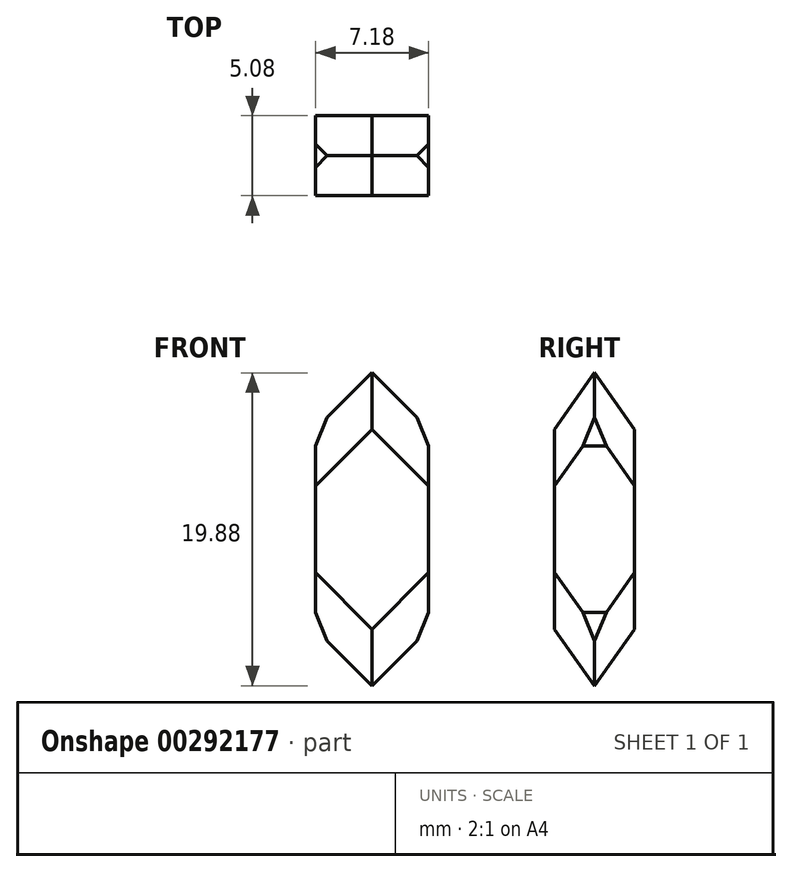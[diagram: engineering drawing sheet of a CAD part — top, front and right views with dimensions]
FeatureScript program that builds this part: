
annotation { "Feature Type Name" : "Feature", "Feature Type Description" : "" }
export const myFeature = defineFeature(function(context is Context, id is Id, definition is map)
    precondition{}
    {
        {
            var Q0;
            Q0=qCreatedBy(makeId("Front.planeOp"),FACE);
            var sketch = newSketch(context, id + "F0", { "sketchPlane" : qUnion([Q0])});
            skLineSegment(sketch, "E0", {"start": v(-22.12, 0) * mm, "end": v(-18.53, 3.6) * mm});
            skLineSegment(sketch, "E1", {"start": v(-18.53, 3.6) * mm, "end": v(-18.53, 16.3) * mm});
            skLineSegment(sketch, "E2", {"start": v(-18.53, 16.3) * mm, "end": v(-22.12, 19.88) * mm});
            skLineSegment(sketch, "E3", {"start": v(-22.12, 19.88) * mm, "end": v(-25.71, 16.3) * mm});
            skLineSegment(sketch, "E4", {"start": v(-25.71, 16.3) * mm, "end": v(-25.71, 3.6) * mm});
            skLineSegment(sketch, "E5", {"start": v(-25.71, 3.6) * mm, "end": v(-22.12, 0) * mm});
            skSolve(sketch);
        }
        {
            var Q0;
            Q0 = qSketchRegion(id + "F0", true);
            extrude(context, id + "F1", {"entities" : qUnion([Q0]), "depth" : 5.08 * mm});
        }
        {
            var Q0;
            Q0=makeQuery(id+"F1.opExtrude","CAP_EDGE",EDGE,{"disambiguationData":[OSD([sQuery(id+"F0.wireOp",EDGE,"E2")])],"isStart":false});
            var Q1;
            Q1=makeQuery(id+"F1.opExtrude","CAP_EDGE",EDGE,{"disambiguationData":[OSD([sQuery(id+"F0.wireOp",EDGE,"E3")])],"isStart":false});
            var Q2;
            Q2=makeQuery(id+"F1.opExtrude","CAP_EDGE",EDGE,{"disambiguationData":[OSD([sQuery(id+"F0.wireOp",EDGE,"E5")])],"isStart":false});
            var Q3;
            Q3=makeQuery(id+"F1.opExtrude","CAP_EDGE",EDGE,{"disambiguationData":[OSD([sQuery(id+"F0.wireOp",EDGE,"E0")])],"isStart":false});
            var Q4;
            Q4=makeQuery(id+"F1.opExtrude","CAP_EDGE",EDGE,{"disambiguationData":[OSD([sQuery(id+"F0.wireOp",EDGE,"E2")])],"isStart":true});
            var Q5;
            Q5=makeQuery(id+"F1.opExtrude","CAP_EDGE",EDGE,{"disambiguationData":[OSD([sQuery(id+"F0.wireOp",EDGE,"E3")])],"isStart":true});
            var Q6;
            Q6=makeQuery(id+"F1.opExtrude","CAP_EDGE",EDGE,{"disambiguationData":[OSD([sQuery(id+"F0.wireOp",EDGE,"E5")])],"isStart":true});
            var Q7;
            Q7=makeQuery(id+"F1.opExtrude","CAP_EDGE",EDGE,{"disambiguationData":[OSD([sQuery(id+"F0.wireOp",EDGE,"E0")])],"isStart":true});
            var Q8;
            Q8=makeQuery(id+"F1.opExtrude","SWEPT_EDGE",EDGE,{"disambiguationData":[OSD([sQuery(id+"F0.wireOp",EDGE,"E0"),sQuery(id+"F0.wireOp",EDGE,"E1")])]});
            var Q9;
            Q9=makeQuery(id+"F1.opExtrude","SWEPT_EDGE",EDGE,{"disambiguationData":[OSD([sQuery(id+"F0.wireOp",EDGE,"E1"),sQuery(id+"F0.wireOp",EDGE,"E2")])]});
            var Q10;
            Q10=makeQuery(id+"F1.opExtrude","SWEPT_EDGE",EDGE,{"disambiguationData":[OSD([sQuery(id+"F0.wireOp",EDGE,"E3"),sQuery(id+"F0.wireOp",EDGE,"E4")])]});
            var Q11;
            Q11=makeQuery(id+"F1.opExtrude","SWEPT_EDGE",EDGE,{"disambiguationData":[OSD([sQuery(id+"F0.wireOp",EDGE,"E4"),sQuery(id+"F0.wireOp",EDGE,"E5")])]});
            chamfer(context, id + "F2", {"entities" : qUnion([Q0, Q1, Q2, Q3, Q4, Q5, Q6, Q7, Q8, Q9, Q10, Q11]), "width" : 2.54 * mm, "tangentPropagation" : true});
        }
    });
